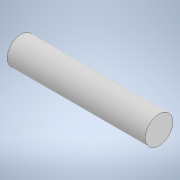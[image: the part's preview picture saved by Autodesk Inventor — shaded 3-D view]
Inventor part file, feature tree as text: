
AUTODESK INVENTOR PART (.ipt)
format: ipt  version: 2022.1 (Build 261234000, 234)  size: 91,648 bytes
history: native  units: mm
features: other x1, extrude x1, sketch x1
ambient origin geometry x8: Origin, YZ Plane, XZ Plane, XY Plane, X Axis, Y Axis, Z Axis, Center Point
bodies: Body1 (feature_tree)
feature tree (3):
  other  "Sólido1"
  extrude  "Extrusión1"  Depth=100.0mm TaperAngle=0.0deg
  sketch  "Boceto1"  dims[d0=20.0mm d1=100.0mm d2=0.0mm]
